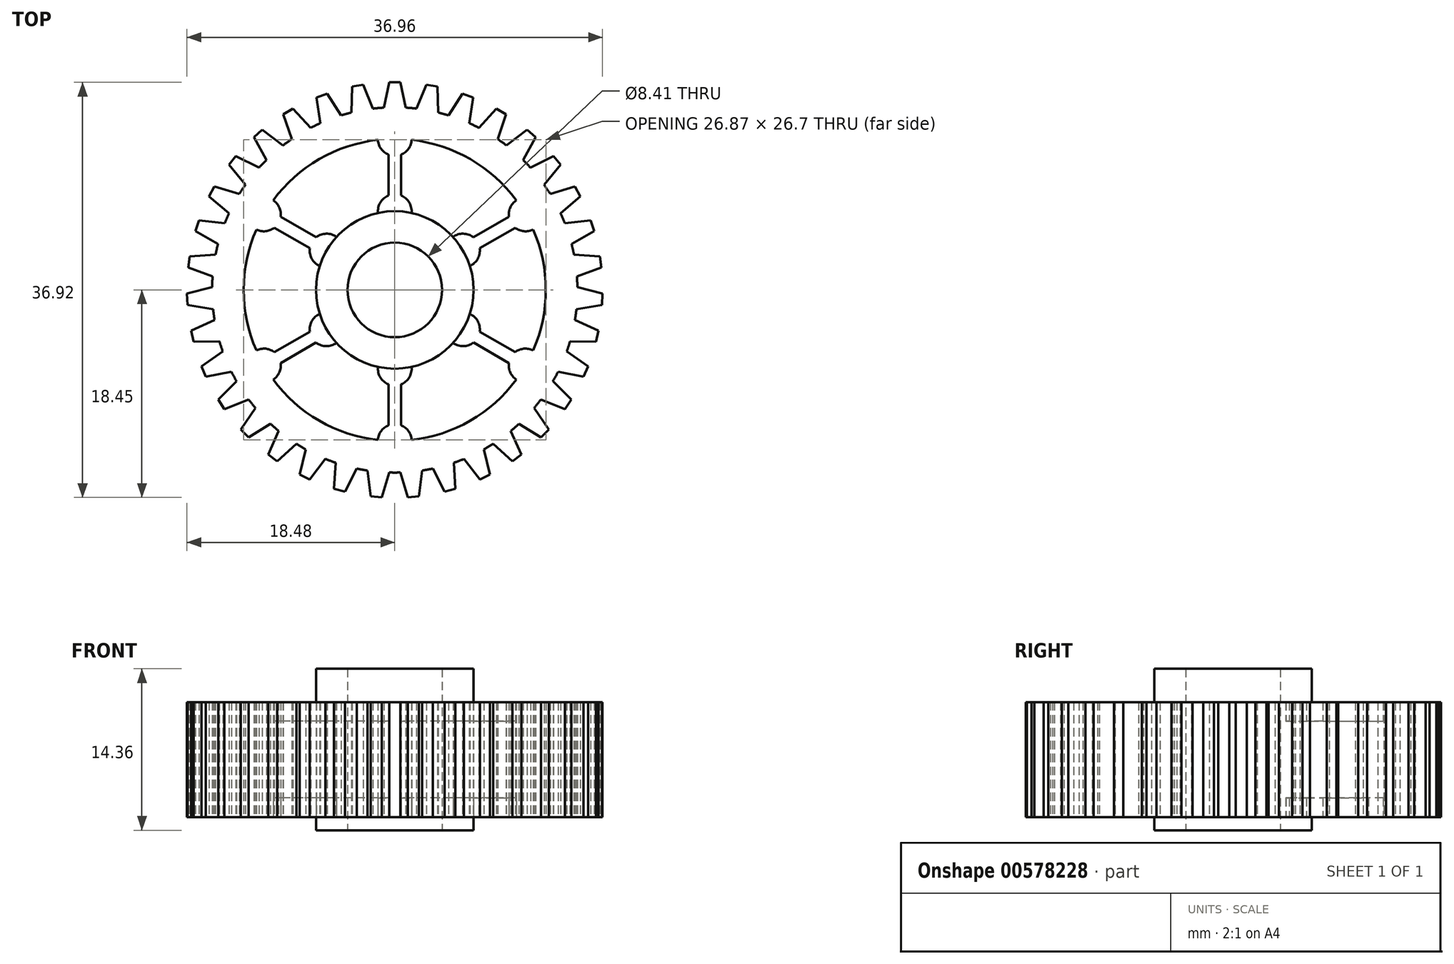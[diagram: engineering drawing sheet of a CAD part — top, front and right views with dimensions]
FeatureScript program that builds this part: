
annotation { "Feature Type Name" : "Feature", "Feature Type Description" : "" }
export const myFeature = defineFeature(function(context is Context, id is Id, definition is map)
    precondition{}
    {
        {
            var Q0;
            Q0=qCreatedBy(makeId("Top.planeOp"),FACE);
            var sketch = newSketch(context, id + "F0", { "sketchPlane" : qUnion([Q0])});
            skCircle(sketch, "E0", {"center": v(0, 0) * mm, "radius": 4.2 * mm});
            skCircle(sketch, "E1.0", {"center": v(0, 0) * mm, "radius": 7 * mm});
            skCircle(sketch, "E2.0", {"center": v(0, 0) * mm, "radius": 16.24 * mm});
            skCircle(sketch, "E3.0", {"center": v(0, 0) * mm, "radius": 13.43 * mm});
            skLineSegment(sketch, "E4", {"start": v(0, 0) * mm, "end": v(0, 25.5) * mm, "construction": true});
            skLineSegment(sketch, "E5", {"start": v(0, 13.43) * mm, "end": v(0, 18.47) * mm});
            skLineSegment(sketch, "E6", {"start": v(0, 18.47) * mm, "end": v(-0.5, 18.47) * mm});
            skLineSegment(sketch, "E7", {"start": v(-0.5, 18.47) * mm, "end": v(-0.98, 16.22) * mm});
            skLineSegment(sketch, "E8", {"start": v(0, 18.47) * mm, "end": v(0.5, 18.47) * mm});
            skLineSegment(sketch, "E9", {"start": v(0.5, 18.47) * mm, "end": v(0.97, 16.22) * mm});
            skLineSegment(sketch, "E10.1.0", {"start": v(-2.8, 18.27) * mm, "end": v(-1.94, 16.13) * mm});
            skLineSegment(sketch, "E10.1.1", {"start": v(-3.3, 18.18) * mm, "end": v(-2.8, 18.27) * mm});
            skLineSegment(sketch, "E10.1.2", {"start": v(-3.3, 18.18) * mm, "end": v(-3.8, 18.09) * mm});
            skLineSegment(sketch, "E10.1.3", {"start": v(-3.8, 18.09) * mm, "end": v(-3.85, 15.78) * mm});
            skLineSegment(sketch, "E10.2.0", {"start": v(-6.02, 17.47) * mm, "end": v(-4.78, 15.52) * mm});
            skLineSegment(sketch, "E10.2.1", {"start": v(-6.5, 17.3) * mm, "end": v(-6.02, 17.47) * mm});
            skLineSegment(sketch, "E10.2.2", {"start": v(-6.5, 17.3) * mm, "end": v(-6.96, 17.12) * mm});
            skLineSegment(sketch, "E10.2.3", {"start": v(-6.96, 17.12) * mm, "end": v(-6.61, 14.84) * mm});
            skLineSegment(sketch, "E10.3.0", {"start": v(-9.05, 16.12) * mm, "end": v(-7.48, 14.42) * mm});
            skLineSegment(sketch, "E10.3.1", {"start": v(-9.48, 15.86) * mm, "end": v(-9.05, 16.12) * mm});
            skLineSegment(sketch, "E10.3.2", {"start": v(-9.48, 15.86) * mm, "end": v(-9.9, 15.6) * mm});
            skLineSegment(sketch, "E10.3.3", {"start": v(-9.9, 15.6) * mm, "end": v(-9.15, 13.42) * mm});
            skLineSegment(sketch, "E10.4.0", {"start": v(-11.78, 14.24) * mm, "end": v(-9.93, 12.85) * mm});
            skLineSegment(sketch, "E10.4.1", {"start": v(-12.16, 13.91) * mm, "end": v(-11.78, 14.24) * mm});
            skLineSegment(sketch, "E10.4.2", {"start": v(-12.16, 13.91) * mm, "end": v(-12.53, 13.58) * mm});
            skLineSegment(sketch, "E10.4.3", {"start": v(-12.53, 13.58) * mm, "end": v(-11.4, 11.57) * mm});
            skLineSegment(sketch, "E10.5.0", {"start": v(-14.13, 11.9) * mm, "end": v(-12.07, 10.87) * mm});
            skLineSegment(sketch, "E10.5.1", {"start": v(-14.44, 11.52) * mm, "end": v(-14.13, 11.9) * mm});
            skLineSegment(sketch, "E10.5.2", {"start": v(-14.44, 11.52) * mm, "end": v(-14.76, 11.13) * mm});
            skLineSegment(sketch, "E10.5.3", {"start": v(-14.76, 11.13) * mm, "end": v(-13.29, 9.35) * mm});
            skLineSegment(sketch, "E10.6.0", {"start": v(-16.03, 9.2) * mm, "end": v(-13.82, 8.54) * mm});
            skLineSegment(sketch, "E10.6.1", {"start": v(-16.27, 8.75) * mm, "end": v(-16.03, 9.2) * mm});
            skLineSegment(sketch, "E10.6.2", {"start": v(-16.27, 8.75) * mm, "end": v(-16.5, 8.31) * mm});
            skLineSegment(sketch, "E10.6.3", {"start": v(-16.5, 8.31) * mm, "end": v(-14.74, 6.83) * mm});
            skLineSegment(sketch, "E10.7.0", {"start": v(-17.42, 6.18) * mm, "end": v(-15.12, 5.94) * mm});
            skLineSegment(sketch, "E10.7.1", {"start": v(-17.57, 5.7) * mm, "end": v(-17.42, 6.18) * mm});
            skLineSegment(sketch, "E10.7.2", {"start": v(-17.57, 5.7) * mm, "end": v(-17.73, 5.23) * mm});
            skLineSegment(sketch, "E10.7.3", {"start": v(-17.73, 5.23) * mm, "end": v(-15.72, 4.08) * mm});
            skLineSegment(sketch, "E10.8.0", {"start": v(-18.24, 2.98) * mm, "end": v(-15.94, 3.14) * mm});
            skLineSegment(sketch, "E10.8.1", {"start": v(-18.3, 2.48) * mm, "end": v(-18.24, 2.98) * mm});
            skLineSegment(sketch, "E10.8.2", {"start": v(-18.3, 2.48) * mm, "end": v(-18.37, 1.98) * mm});
            skLineSegment(sketch, "E10.8.3", {"start": v(-18.37, 1.98) * mm, "end": v(-16.2, 1.21) * mm});
            skLineSegment(sketch, "E10.9.0", {"start": v(-18.48, -0.33) * mm, "end": v(-16.24, 0.25) * mm});
            skLineSegment(sketch, "E10.9.1", {"start": v(-18.46, -0.83) * mm, "end": v(-18.48, -0.33) * mm});
            skLineSegment(sketch, "E10.9.2", {"start": v(-18.46, -0.83) * mm, "end": v(-18.43, -1.33) * mm});
            skLineSegment(sketch, "E10.9.3", {"start": v(-18.43, -1.33) * mm, "end": v(-16.16, -1.7) * mm});
            skLineSegment(sketch, "E10.10.0", {"start": v(-18.12, -3.62) * mm, "end": v(-16.03, -2.66) * mm});
            skLineSegment(sketch, "E10.10.1", {"start": v(-18.01, -4.11) * mm, "end": v(-18.12, -3.62) * mm});
            skLineSegment(sketch, "E10.10.2", {"start": v(-18.01, -4.11) * mm, "end": v(-17.9, -4.6) * mm});
            skLineSegment(sketch, "E10.10.3", {"start": v(-17.9, -4.6) * mm, "end": v(-15.6, -4.56) * mm});
            skLineSegment(sketch, "E10.11.0", {"start": v(-17.18, -6.8) * mm, "end": v(-15.3, -5.48) * mm});
            skLineSegment(sketch, "E10.11.1", {"start": v(-16.99, -7.26) * mm, "end": v(-17.18, -6.8) * mm});
            skLineSegment(sketch, "E10.11.2", {"start": v(-16.99, -7.26) * mm, "end": v(-16.8, -7.72) * mm});
            skLineSegment(sketch, "E10.11.3", {"start": v(-16.8, -7.72) * mm, "end": v(-14.53, -7.27) * mm});
            skLineSegment(sketch, "E10.12.0", {"start": v(-15.7, -9.76) * mm, "end": v(-14.07, -8.12) * mm});
            skLineSegment(sketch, "E10.12.1", {"start": v(-15.42, -10.18) * mm, "end": v(-15.7, -9.76) * mm});
            skLineSegment(sketch, "E10.12.2", {"start": v(-15.42, -10.18) * mm, "end": v(-15.14, -10.6) * mm});
            skLineSegment(sketch, "E10.12.3", {"start": v(-15.14, -10.6) * mm, "end": v(-13, -9.75) * mm});
            skLineSegment(sketch, "E10.13.0", {"start": v(-13.7, -12.4) * mm, "end": v(-12.4, -10.5) * mm});
            skLineSegment(sketch, "E10.13.1", {"start": v(-13.35, -12.77) * mm, "end": v(-13.7, -12.4) * mm});
            skLineSegment(sketch, "E10.13.2", {"start": v(-13.35, -12.77) * mm, "end": v(-13, -13.13) * mm});
            skLineSegment(sketch, "E10.13.3", {"start": v(-13, -13.13) * mm, "end": v(-11.05, -11.91) * mm});
            skLineSegment(sketch, "E10.14.0", {"start": v(-11.26, -14.65) * mm, "end": v(-10.32, -12.55) * mm});
            skLineSegment(sketch, "E10.14.1", {"start": v(-10.86, -14.95) * mm, "end": v(-11.26, -14.65) * mm});
            skLineSegment(sketch, "E10.14.2", {"start": v(-10.86, -14.95) * mm, "end": v(-10.45, -15.24) * mm});
            skLineSegment(sketch, "E10.14.3", {"start": v(-10.45, -15.24) * mm, "end": v(-8.74, -13.7) * mm});
            skLineSegment(sketch, "E10.15.0", {"start": v(-8.47, -16.43) * mm, "end": v(-7.91, -14.19) * mm});
            skLineSegment(sketch, "E10.15.1", {"start": v(-8.02, -16.65) * mm, "end": v(-8.47, -16.43) * mm});
            skLineSegment(sketch, "E10.15.2", {"start": v(-8.02, -16.65) * mm, "end": v(-7.57, -16.86) * mm});
            skLineSegment(sketch, "E10.15.3", {"start": v(-7.57, -16.86) * mm, "end": v(-6.16, -15.03) * mm});
            skLineSegment(sketch, "E10.16.0", {"start": v(-5.4, -17.68) * mm, "end": v(-5.25, -15.37) * mm});
            skLineSegment(sketch, "E10.16.1", {"start": v(-4.92, -17.8) * mm, "end": v(-5.4, -17.68) * mm});
            skLineSegment(sketch, "E10.16.2", {"start": v(-4.92, -17.8) * mm, "end": v(-4.43, -17.94) * mm});
            skLineSegment(sketch, "E10.16.3", {"start": v(-4.43, -17.94) * mm, "end": v(-3.37, -15.9) * mm});
            skLineSegment(sketch, "E10.17.0", {"start": v(-2.15, -18.36) * mm, "end": v(-2.42, -16.06) * mm});
            skLineSegment(sketch, "E10.17.1", {"start": v(-1.66, -18.4) * mm, "end": v(-2.15, -18.36) * mm});
            skLineSegment(sketch, "E10.17.2", {"start": v(-1.66, -18.4) * mm, "end": v(-1.16, -18.45) * mm});
            skLineSegment(sketch, "E10.17.3", {"start": v(-1.16, -18.45) * mm, "end": v(-0.48, -16.24) * mm});
            skLineSegment(sketch, "E10.18.0", {"start": v(1.16, -18.45) * mm, "end": v(0.48, -16.24) * mm});
            skLineSegment(sketch, "E10.18.1", {"start": v(1.66, -18.4) * mm, "end": v(1.16, -18.45) * mm});
            skLineSegment(sketch, "E10.18.2", {"start": v(1.66, -18.4) * mm, "end": v(2.15, -18.36) * mm});
            skLineSegment(sketch, "E10.18.3", {"start": v(2.15, -18.36) * mm, "end": v(2.42, -16.06) * mm});
            skLineSegment(sketch, "E10.19.0", {"start": v(4.43, -17.94) * mm, "end": v(3.37, -15.9) * mm});
            skLineSegment(sketch, "E10.19.1", {"start": v(4.92, -17.8) * mm, "end": v(4.43, -17.94) * mm});
            skLineSegment(sketch, "E10.19.2", {"start": v(4.92, -17.8) * mm, "end": v(5.4, -17.68) * mm});
            skLineSegment(sketch, "E10.19.3", {"start": v(5.4, -17.68) * mm, "end": v(5.25, -15.37) * mm});
            skLineSegment(sketch, "E10.20.0", {"start": v(7.57, -16.86) * mm, "end": v(6.16, -15.03) * mm});
            skLineSegment(sketch, "E10.20.1", {"start": v(8.02, -16.65) * mm, "end": v(7.57, -16.86) * mm});
            skLineSegment(sketch, "E10.20.2", {"start": v(8.02, -16.65) * mm, "end": v(8.47, -16.43) * mm});
            skLineSegment(sketch, "E10.20.3", {"start": v(8.47, -16.43) * mm, "end": v(7.91, -14.19) * mm});
            skLineSegment(sketch, "E10.21.0", {"start": v(10.45, -15.24) * mm, "end": v(8.74, -13.7) * mm});
            skLineSegment(sketch, "E10.21.1", {"start": v(10.86, -14.95) * mm, "end": v(10.45, -15.24) * mm});
            skLineSegment(sketch, "E10.21.2", {"start": v(10.86, -14.95) * mm, "end": v(11.26, -14.65) * mm});
            skLineSegment(sketch, "E10.21.3", {"start": v(11.26, -14.65) * mm, "end": v(10.32, -12.55) * mm});
            skLineSegment(sketch, "E10.22.0", {"start": v(13, -13.13) * mm, "end": v(11.05, -11.91) * mm});
            skLineSegment(sketch, "E10.22.1", {"start": v(13.35, -12.77) * mm, "end": v(13, -13.13) * mm});
            skLineSegment(sketch, "E10.22.2", {"start": v(13.35, -12.77) * mm, "end": v(13.7, -12.4) * mm});
            skLineSegment(sketch, "E10.22.3", {"start": v(13.7, -12.4) * mm, "end": v(12.4, -10.5) * mm});
            skLineSegment(sketch, "E10.23.0", {"start": v(15.14, -10.6) * mm, "end": v(13, -9.75) * mm});
            skLineSegment(sketch, "E10.23.1", {"start": v(15.42, -10.18) * mm, "end": v(15.14, -10.6) * mm});
            skLineSegment(sketch, "E10.23.2", {"start": v(15.42, -10.18) * mm, "end": v(15.7, -9.76) * mm});
            skLineSegment(sketch, "E10.23.3", {"start": v(15.7, -9.76) * mm, "end": v(14.07, -8.12) * mm});
            skLineSegment(sketch, "E10.24.0", {"start": v(16.8, -7.72) * mm, "end": v(14.53, -7.27) * mm});
            skLineSegment(sketch, "E10.24.1", {"start": v(16.99, -7.26) * mm, "end": v(16.8, -7.72) * mm});
            skLineSegment(sketch, "E10.24.2", {"start": v(16.99, -7.26) * mm, "end": v(17.18, -6.8) * mm});
            skLineSegment(sketch, "E10.24.3", {"start": v(17.18, -6.8) * mm, "end": v(15.3, -5.48) * mm});
            skLineSegment(sketch, "E10.25.0", {"start": v(17.9, -4.6) * mm, "end": v(15.6, -4.56) * mm});
            skLineSegment(sketch, "E10.25.1", {"start": v(18.01, -4.11) * mm, "end": v(17.9, -4.6) * mm});
            skLineSegment(sketch, "E10.25.2", {"start": v(18.01, -4.11) * mm, "end": v(18.12, -3.62) * mm});
            skLineSegment(sketch, "E10.25.3", {"start": v(18.12, -3.62) * mm, "end": v(16.03, -2.66) * mm});
            skLineSegment(sketch, "E10.26.0", {"start": v(18.43, -1.33) * mm, "end": v(16.16, -1.7) * mm});
            skLineSegment(sketch, "E10.26.1", {"start": v(18.46, -0.83) * mm, "end": v(18.43, -1.33) * mm});
            skLineSegment(sketch, "E10.26.2", {"start": v(18.46, -0.83) * mm, "end": v(18.48, -0.33) * mm});
            skLineSegment(sketch, "E10.26.3", {"start": v(18.48, -0.33) * mm, "end": v(16.24, 0.25) * mm});
            skLineSegment(sketch, "E10.27.0", {"start": v(18.37, 1.98) * mm, "end": v(16.2, 1.21) * mm});
            skLineSegment(sketch, "E10.27.1", {"start": v(18.3, 2.48) * mm, "end": v(18.37, 1.98) * mm});
            skLineSegment(sketch, "E10.27.2", {"start": v(18.3, 2.48) * mm, "end": v(18.24, 2.98) * mm});
            skLineSegment(sketch, "E10.27.3", {"start": v(18.24, 2.98) * mm, "end": v(15.94, 3.14) * mm});
            skLineSegment(sketch, "E10.28.0", {"start": v(17.73, 5.23) * mm, "end": v(15.72, 4.08) * mm});
            skLineSegment(sketch, "E10.28.1", {"start": v(17.57, 5.7) * mm, "end": v(17.73, 5.23) * mm});
            skLineSegment(sketch, "E10.28.2", {"start": v(17.57, 5.7) * mm, "end": v(17.42, 6.18) * mm});
            skLineSegment(sketch, "E10.28.3", {"start": v(17.42, 6.18) * mm, "end": v(15.12, 5.94) * mm});
            skLineSegment(sketch, "E10.29.0", {"start": v(16.5, 8.31) * mm, "end": v(14.74, 6.83) * mm});
            skLineSegment(sketch, "E10.29.1", {"start": v(16.27, 8.75) * mm, "end": v(16.5, 8.31) * mm});
            skLineSegment(sketch, "E10.29.2", {"start": v(16.27, 8.75) * mm, "end": v(16.03, 9.2) * mm});
            skLineSegment(sketch, "E10.29.3", {"start": v(16.03, 9.2) * mm, "end": v(13.82, 8.54) * mm});
            skLineSegment(sketch, "E10.30.0", {"start": v(14.76, 11.13) * mm, "end": v(13.29, 9.35) * mm});
            skLineSegment(sketch, "E10.30.1", {"start": v(14.44, 11.52) * mm, "end": v(14.76, 11.13) * mm});
            skLineSegment(sketch, "E10.30.2", {"start": v(14.44, 11.52) * mm, "end": v(14.13, 11.9) * mm});
            skLineSegment(sketch, "E10.30.3", {"start": v(14.13, 11.9) * mm, "end": v(12.07, 10.87) * mm});
            skLineSegment(sketch, "E10.31.0", {"start": v(12.53, 13.58) * mm, "end": v(11.4, 11.57) * mm});
            skLineSegment(sketch, "E10.31.1", {"start": v(12.16, 13.91) * mm, "end": v(12.53, 13.58) * mm});
            skLineSegment(sketch, "E10.31.2", {"start": v(12.16, 13.91) * mm, "end": v(11.78, 14.24) * mm});
            skLineSegment(sketch, "E10.31.3", {"start": v(11.78, 14.24) * mm, "end": v(9.93, 12.85) * mm});
            skLineSegment(sketch, "E10.32.0", {"start": v(9.9, 15.6) * mm, "end": v(9.15, 13.42) * mm});
            skLineSegment(sketch, "E10.32.1", {"start": v(9.48, 15.86) * mm, "end": v(9.9, 15.6) * mm});
            skLineSegment(sketch, "E10.32.2", {"start": v(9.48, 15.86) * mm, "end": v(9.05, 16.12) * mm});
            skLineSegment(sketch, "E10.32.3", {"start": v(9.05, 16.12) * mm, "end": v(7.48, 14.42) * mm});
            skLineSegment(sketch, "E10.33.0", {"start": v(6.96, 17.12) * mm, "end": v(6.61, 14.84) * mm});
            skLineSegment(sketch, "E10.33.1", {"start": v(6.5, 17.3) * mm, "end": v(6.96, 17.12) * mm});
            skLineSegment(sketch, "E10.33.2", {"start": v(6.5, 17.3) * mm, "end": v(6.02, 17.47) * mm});
            skLineSegment(sketch, "E10.33.3", {"start": v(6.02, 17.47) * mm, "end": v(4.78, 15.52) * mm});
            skLineSegment(sketch, "E10.34.0", {"start": v(3.8, 18.09) * mm, "end": v(3.85, 15.78) * mm});
            skLineSegment(sketch, "E10.34.1", {"start": v(3.3, 18.18) * mm, "end": v(3.8, 18.09) * mm});
            skLineSegment(sketch, "E10.34.2", {"start": v(3.3, 18.18) * mm, "end": v(2.8, 18.27) * mm});
            skLineSegment(sketch, "E10.34.3", {"start": v(2.8, 18.27) * mm, "end": v(1.94, 16.13) * mm});
            skLineSegment(sketch, "E11.left", {"start": v(-0.56, 8.4) * mm, "end": v(-0.56, 12.04) * mm});
            skLineSegment(sketch, "E11.right", {"start": v(0.56, 8.4) * mm, "end": v(0.56, 12.04) * mm});
            skPoint(sketch, "E11.middle", {"position": v(0, 10.27) * mm});
            skArc(sketch, "E12", {"start": v(-1.5, 13.35) * mm, "mid": v(-1.22, 12.56) * mm, "end": v(-0.56, 12.04) * mm});
            skArc(sketch, "E13.trimOffspring", {"start": v(0.56, 12.04) * mm, "mid": v(1.22, 12.56) * mm, "end": v(1.5, 13.35) * mm});
            skArc(sketch, "E14", {"start": v(-1.5, 6.84) * mm, "mid": v(-1.29, 7.78) * mm, "end": v(-0.56, 8.4) * mm});
            skArc(sketch, "E15.trimOffspring", {"start": v(0.56, 8.4) * mm, "mid": v(1.29, 7.78) * mm, "end": v(1.5, 6.84) * mm});
            skArc(sketch, "E16.1.0", {"start": v(-10.15, 6.5) * mm, "mid": v(-10.27, 7.34) * mm, "end": v(-10.81, 7.97) * mm});
            skLineSegment(sketch, "E16.1.1", {"start": v(-7, 4.68) * mm, "end": v(-10.15, 6.5) * mm});
            skArc(sketch, "E16.1.2", {"start": v(-7, 4.68) * mm, "mid": v(-6.1, 5) * mm, "end": v(-5.18, 4.71) * mm});
            skArc(sketch, "E16.1.3", {"start": v(-6.67, 2.13) * mm, "mid": v(-7.38, 2.77) * mm, "end": v(-7.55, 3.71) * mm});
            skLineSegment(sketch, "E16.1.4", {"start": v(-7.55, 3.71) * mm, "end": v(-10.7, 5.54) * mm});
            skArc(sketch, "E16.1.5", {"start": v(-12.31, 5.38) * mm, "mid": v(-11.49, 5.22) * mm, "end": v(-10.7, 5.54) * mm});
            skArc(sketch, "E16.2.0", {"start": v(-10.7, -5.54) * mm, "mid": v(-11.49, -5.22) * mm, "end": v(-12.31, -5.38) * mm});
            skLineSegment(sketch, "E16.2.1", {"start": v(-7.55, -3.71) * mm, "end": v(-10.7, -5.54) * mm});
            skArc(sketch, "E16.2.2", {"start": v(-7.55, -3.71) * mm, "mid": v(-7.38, -2.77) * mm, "end": v(-6.67, -2.13) * mm});
            skArc(sketch, "E16.2.3", {"start": v(-5.18, -4.71) * mm, "mid": v(-6.1, -5) * mm, "end": v(-7, -4.68) * mm});
            skLineSegment(sketch, "E16.2.4", {"start": v(-7, -4.68) * mm, "end": v(-10.15, -6.5) * mm});
            skArc(sketch, "E16.2.5", {"start": v(-10.81, -7.97) * mm, "mid": v(-10.27, -7.34) * mm, "end": v(-10.15, -6.5) * mm});
            skArc(sketch, "E16.3.0", {"start": v(-0.56, -12.04) * mm, "mid": v(-1.22, -12.56) * mm, "end": v(-1.5, -13.35) * mm});
            skLineSegment(sketch, "E16.3.1", {"start": v(-0.56, -8.4) * mm, "end": v(-0.56, -12.04) * mm});
            skArc(sketch, "E16.3.2", {"start": v(-0.56, -8.4) * mm, "mid": v(-1.29, -7.78) * mm, "end": v(-1.5, -6.84) * mm});
            skArc(sketch, "E16.3.3", {"start": v(1.5, -6.84) * mm, "mid": v(1.29, -7.78) * mm, "end": v(0.56, -8.4) * mm});
            skLineSegment(sketch, "E16.3.4", {"start": v(0.56, -8.4) * mm, "end": v(0.56, -12.04) * mm});
            skArc(sketch, "E16.3.5", {"start": v(1.5, -13.35) * mm, "mid": v(1.22, -12.56) * mm, "end": v(0.56, -12.04) * mm});
            skArc(sketch, "E16.4.0", {"start": v(10.15, -6.5) * mm, "mid": v(10.27, -7.34) * mm, "end": v(10.81, -7.97) * mm});
            skLineSegment(sketch, "E16.4.1", {"start": v(7, -4.68) * mm, "end": v(10.15, -6.5) * mm});
            skArc(sketch, "E16.4.2", {"start": v(7, -4.68) * mm, "mid": v(6.1, -5) * mm, "end": v(5.18, -4.71) * mm});
            skArc(sketch, "E16.4.3", {"start": v(6.67, -2.13) * mm, "mid": v(7.38, -2.77) * mm, "end": v(7.55, -3.71) * mm});
            skLineSegment(sketch, "E16.4.4", {"start": v(7.55, -3.71) * mm, "end": v(10.7, -5.54) * mm});
            skArc(sketch, "E16.4.5", {"start": v(12.31, -5.38) * mm, "mid": v(11.49, -5.22) * mm, "end": v(10.7, -5.54) * mm});
            skArc(sketch, "E16.5.0", {"start": v(10.7, 5.54) * mm, "mid": v(11.49, 5.22) * mm, "end": v(12.31, 5.38) * mm});
            skLineSegment(sketch, "E16.5.1", {"start": v(7.55, 3.71) * mm, "end": v(10.7, 5.54) * mm});
            skArc(sketch, "E16.5.2", {"start": v(7.55, 3.71) * mm, "mid": v(7.38, 2.77) * mm, "end": v(6.67, 2.13) * mm});
            skArc(sketch, "E16.5.3", {"start": v(5.18, 4.71) * mm, "mid": v(6.1, 5) * mm, "end": v(7, 4.68) * mm});
            skLineSegment(sketch, "E16.5.4", {"start": v(7, 4.68) * mm, "end": v(10.15, 6.5) * mm});
            skArc(sketch, "E16.5.5", {"start": v(10.81, 7.97) * mm, "mid": v(10.27, 7.34) * mm, "end": v(10.15, 6.5) * mm});
            skSolve(sketch);
        }
        {
            var Q0;
            {var subQ72=sQuery(id+"F0.wireOp",EDGE,"E3.0");var subQ76=makeQuery(id+"F0.imprint","IMPRINT",VERTEX,{"derivedFrom":subQ72});Q0=makeQuery(id+"F0.imprint","IMPRINT",FACE,{"disambiguationData":[TD([[makeQuery(id+"F0.imprint","IMPRINT",EDGE,{"disambiguationData":[TD([[subQ76,1.0]])],"derivedFrom":subQ72}),-1.0]])]});}
            var Q1;
            {var subQ0=sQuery(id+"F0.wireOp",EDGE,"E16.1.0");Q1=makeQuery(id+"F0.imprint","IMPRINT",FACE,{"disambiguationData":[TD([[makeQuery(id+"F0.imprint","IMPRINT",EDGE,{"derivedFrom":subQ0}),1.0]])]});}
            var Q2;
            Q2=makeQuery(id+"F0.imprint","IMPRINT",FACE,{"disambiguationData":[TD([[makeQuery(id+"F0.imprint","IMPRINT",EDGE,{"derivedFrom":sQuery(id+"F0.wireOp",EDGE,"E11.left")}),-1.0]])]});
            var Q3;
            {var subQ0=sQuery(id+"F0.wireOp",EDGE,"E16.5.0");Q3=makeQuery(id+"F0.imprint","IMPRINT",FACE,{"disambiguationData":[TD([[makeQuery(id+"F0.imprint","IMPRINT",EDGE,{"derivedFrom":subQ0}),1.0]])]});}
            var Q4;
            {var subQ0=sQuery(id+"F0.wireOp",EDGE,"E16.4.0");Q4=makeQuery(id+"F0.imprint","IMPRINT",FACE,{"disambiguationData":[TD([[makeQuery(id+"F0.imprint","IMPRINT",EDGE,{"derivedFrom":subQ0}),1.0]])]});}
            var Q5;
            {var subQ0=sQuery(id+"F0.wireOp",EDGE,"E16.3.0");Q5=makeQuery(id+"F0.imprint","IMPRINT",FACE,{"disambiguationData":[TD([[makeQuery(id+"F0.imprint","IMPRINT",EDGE,{"derivedFrom":subQ0}),1.0]])]});}
            var Q6;
            {var subQ0=sQuery(id+"F0.wireOp",EDGE,"E16.2.0");Q6=makeQuery(id+"F0.imprint","IMPRINT",FACE,{"disambiguationData":[TD([[makeQuery(id+"F0.imprint","IMPRINT",EDGE,{"derivedFrom":subQ0}),1.0]])]});}
            var Q7;
            Q7=makeQuery(id+"F0.imprint","IMPRINT",FACE,{"disambiguationData":[TD([[makeQuery(id+"F0.imprint","IMPRINT",EDGE,{"derivedFrom":sQuery(id+"F0.wireOp",EDGE,"E0")}),-1.0]])]});
            var Q8;
            {var subQ0=sQuery(id+"F0.wireOp",EDGE,"E10.5.0");Q8=makeQuery(id+"F0.imprint","IMPRINT",FACE,{"disambiguationData":[TD([[makeQuery(id+"F0.imprint","IMPRINT",EDGE,{"derivedFrom":subQ0}),-1.0]])]});}
            var Q9;
            {var subQ0=sQuery(id+"F0.wireOp",EDGE,"E10.4.0");Q9=makeQuery(id+"F0.imprint","IMPRINT",FACE,{"disambiguationData":[TD([[makeQuery(id+"F0.imprint","IMPRINT",EDGE,{"derivedFrom":subQ0}),-1.0]])]});}
            var Q10;
            {var subQ0=sQuery(id+"F0.wireOp",EDGE,"E10.3.0");Q10=makeQuery(id+"F0.imprint","IMPRINT",FACE,{"disambiguationData":[TD([[makeQuery(id+"F0.imprint","IMPRINT",EDGE,{"derivedFrom":subQ0}),-1.0]])]});}
            var Q11;
            {var subQ0=sQuery(id+"F0.wireOp",EDGE,"E10.2.0");Q11=makeQuery(id+"F0.imprint","IMPRINT",FACE,{"disambiguationData":[TD([[makeQuery(id+"F0.imprint","IMPRINT",EDGE,{"derivedFrom":subQ0}),-1.0]])]});}
            var Q12;
            {var subQ0=sQuery(id+"F0.wireOp",EDGE,"E10.1.0");Q12=makeQuery(id+"F0.imprint","IMPRINT",FACE,{"disambiguationData":[TD([[makeQuery(id+"F0.imprint","IMPRINT",EDGE,{"derivedFrom":subQ0}),-1.0]])]});}
            var Q13;
            {var subQ0=sQuery(id+"F0.wireOp",EDGE,"E10.9.0");Q13=makeQuery(id+"F0.imprint","IMPRINT",FACE,{"disambiguationData":[TD([[makeQuery(id+"F0.imprint","IMPRINT",EDGE,{"derivedFrom":subQ0}),-1.0]])]});}
            var Q14;
            {var subQ0=sQuery(id+"F0.wireOp",EDGE,"E10.10.0");Q14=makeQuery(id+"F0.imprint","IMPRINT",FACE,{"disambiguationData":[TD([[makeQuery(id+"F0.imprint","IMPRINT",EDGE,{"derivedFrom":subQ0}),-1.0]])]});}
            var Q15;
            {var subQ0=sQuery(id+"F0.wireOp",EDGE,"E10.16.0");Q15=makeQuery(id+"F0.imprint","IMPRINT",FACE,{"disambiguationData":[TD([[makeQuery(id+"F0.imprint","IMPRINT",EDGE,{"derivedFrom":subQ0}),-1.0]])]});}
            var Q16;
            {var subQ0=sQuery(id+"F0.wireOp",EDGE,"E10.11.0");Q16=makeQuery(id+"F0.imprint","IMPRINT",FACE,{"disambiguationData":[TD([[makeQuery(id+"F0.imprint","IMPRINT",EDGE,{"derivedFrom":subQ0}),-1.0]])]});}
            var Q17;
            {var subQ0=sQuery(id+"F0.wireOp",EDGE,"E10.26.0");Q17=makeQuery(id+"F0.imprint","IMPRINT",FACE,{"disambiguationData":[TD([[makeQuery(id+"F0.imprint","IMPRINT",EDGE,{"derivedFrom":subQ0}),-1.0]])]});}
            var Q18;
            {var subQ4=sQuery(id+"F0.wireOp",EDGE,"E8");Q18=makeQuery(id+"F0.imprint","IMPRINT",FACE,{"disambiguationData":[TD([[makeQuery(id+"F0.imprint","IMPRINT",EDGE,{"derivedFrom":subQ4}),-1.0]])]});}
            var Q19;
            {var subQ0=sQuery(id+"F0.wireOp",EDGE,"E10.25.0");Q19=makeQuery(id+"F0.imprint","IMPRINT",FACE,{"disambiguationData":[TD([[makeQuery(id+"F0.imprint","IMPRINT",EDGE,{"derivedFrom":subQ0}),-1.0]])]});}
            var Q20;
            {var subQ0=sQuery(id+"F0.wireOp",EDGE,"E10.12.0");Q20=makeQuery(id+"F0.imprint","IMPRINT",FACE,{"disambiguationData":[TD([[makeQuery(id+"F0.imprint","IMPRINT",EDGE,{"derivedFrom":subQ0}),-1.0]])]});}
            var Q21;
            {var subQ4=sQuery(id+"F0.wireOp",EDGE,"E6");Q21=makeQuery(id+"F0.imprint","IMPRINT",FACE,{"disambiguationData":[TD([[makeQuery(id+"F0.imprint","IMPRINT",EDGE,{"derivedFrom":subQ4}),1.0]])]});}
            var Q22;
            {var subQ0=sQuery(id+"F0.wireOp",EDGE,"E10.20.0");Q22=makeQuery(id+"F0.imprint","IMPRINT",FACE,{"disambiguationData":[TD([[makeQuery(id+"F0.imprint","IMPRINT",EDGE,{"derivedFrom":subQ0}),-1.0]])]});}
            var Q23;
            {var subQ0=sQuery(id+"F0.wireOp",EDGE,"E10.13.0");Q23=makeQuery(id+"F0.imprint","IMPRINT",FACE,{"disambiguationData":[TD([[makeQuery(id+"F0.imprint","IMPRINT",EDGE,{"derivedFrom":subQ0}),-1.0]])]});}
            var Q24;
            {var subQ0=sQuery(id+"F0.wireOp",EDGE,"E10.7.0");Q24=makeQuery(id+"F0.imprint","IMPRINT",FACE,{"disambiguationData":[TD([[makeQuery(id+"F0.imprint","IMPRINT",EDGE,{"derivedFrom":subQ0}),-1.0]])]});}
            var Q25;
            {var subQ0=sQuery(id+"F0.wireOp",EDGE,"E10.14.0");Q25=makeQuery(id+"F0.imprint","IMPRINT",FACE,{"disambiguationData":[TD([[makeQuery(id+"F0.imprint","IMPRINT",EDGE,{"derivedFrom":subQ0}),-1.0]])]});}
            var Q26;
            {var subQ0=sQuery(id+"F0.wireOp",EDGE,"E10.30.0");Q26=makeQuery(id+"F0.imprint","IMPRINT",FACE,{"disambiguationData":[TD([[makeQuery(id+"F0.imprint","IMPRINT",EDGE,{"derivedFrom":subQ0}),-1.0]])]});}
            var Q27;
            {var subQ0=sQuery(id+"F0.wireOp",EDGE,"E10.28.0");Q27=makeQuery(id+"F0.imprint","IMPRINT",FACE,{"disambiguationData":[TD([[makeQuery(id+"F0.imprint","IMPRINT",EDGE,{"derivedFrom":subQ0}),-1.0]])]});}
            var Q28;
            {var subQ0=sQuery(id+"F0.wireOp",EDGE,"E10.24.0");Q28=makeQuery(id+"F0.imprint","IMPRINT",FACE,{"disambiguationData":[TD([[makeQuery(id+"F0.imprint","IMPRINT",EDGE,{"derivedFrom":subQ0}),-1.0]])]});}
            var Q29;
            {var subQ0=sQuery(id+"F0.wireOp",EDGE,"E10.8.0");Q29=makeQuery(id+"F0.imprint","IMPRINT",FACE,{"disambiguationData":[TD([[makeQuery(id+"F0.imprint","IMPRINT",EDGE,{"derivedFrom":subQ0}),-1.0]])]});}
            var Q30;
            {var subQ0=sQuery(id+"F0.wireOp",EDGE,"E10.23.0");Q30=makeQuery(id+"F0.imprint","IMPRINT",FACE,{"disambiguationData":[TD([[makeQuery(id+"F0.imprint","IMPRINT",EDGE,{"derivedFrom":subQ0}),-1.0]])]});}
            var Q31;
            {var subQ0=sQuery(id+"F0.wireOp",EDGE,"E10.27.0");Q31=makeQuery(id+"F0.imprint","IMPRINT",FACE,{"disambiguationData":[TD([[makeQuery(id+"F0.imprint","IMPRINT",EDGE,{"derivedFrom":subQ0}),-1.0]])]});}
            var Q32;
            {var subQ0=sQuery(id+"F0.wireOp",EDGE,"E10.31.0");Q32=makeQuery(id+"F0.imprint","IMPRINT",FACE,{"disambiguationData":[TD([[makeQuery(id+"F0.imprint","IMPRINT",EDGE,{"derivedFrom":subQ0}),-1.0]])]});}
            var Q33;
            {var subQ0=sQuery(id+"F0.wireOp",EDGE,"E10.17.0");Q33=makeQuery(id+"F0.imprint","IMPRINT",FACE,{"disambiguationData":[TD([[makeQuery(id+"F0.imprint","IMPRINT",EDGE,{"derivedFrom":subQ0}),-1.0]])]});}
            var Q34;
            {var subQ0=sQuery(id+"F0.wireOp",EDGE,"E10.32.0");Q34=makeQuery(id+"F0.imprint","IMPRINT",FACE,{"disambiguationData":[TD([[makeQuery(id+"F0.imprint","IMPRINT",EDGE,{"derivedFrom":subQ0}),-1.0]])]});}
            var Q35;
            {var subQ0=sQuery(id+"F0.wireOp",EDGE,"E10.33.0");Q35=makeQuery(id+"F0.imprint","IMPRINT",FACE,{"disambiguationData":[TD([[makeQuery(id+"F0.imprint","IMPRINT",EDGE,{"derivedFrom":subQ0}),-1.0]])]});}
            var Q36;
            {var subQ0=sQuery(id+"F0.wireOp",EDGE,"E10.34.0");Q36=makeQuery(id+"F0.imprint","IMPRINT",FACE,{"disambiguationData":[TD([[makeQuery(id+"F0.imprint","IMPRINT",EDGE,{"derivedFrom":subQ0}),-1.0]])]});}
            var Q37;
            {var subQ0=sQuery(id+"F0.wireOp",EDGE,"E10.29.0");Q37=makeQuery(id+"F0.imprint","IMPRINT",FACE,{"disambiguationData":[TD([[makeQuery(id+"F0.imprint","IMPRINT",EDGE,{"derivedFrom":subQ0}),-1.0]])]});}
            var Q38;
            {var subQ0=sQuery(id+"F0.wireOp",EDGE,"E10.6.0");Q38=makeQuery(id+"F0.imprint","IMPRINT",FACE,{"disambiguationData":[TD([[makeQuery(id+"F0.imprint","IMPRINT",EDGE,{"derivedFrom":subQ0}),-1.0]])]});}
            var Q39;
            {var subQ0=sQuery(id+"F0.wireOp",EDGE,"E10.15.0");Q39=makeQuery(id+"F0.imprint","IMPRINT",FACE,{"disambiguationData":[TD([[makeQuery(id+"F0.imprint","IMPRINT",EDGE,{"derivedFrom":subQ0}),-1.0]])]});}
            var Q40;
            {var subQ0=sQuery(id+"F0.wireOp",EDGE,"E10.22.0");Q40=makeQuery(id+"F0.imprint","IMPRINT",FACE,{"disambiguationData":[TD([[makeQuery(id+"F0.imprint","IMPRINT",EDGE,{"derivedFrom":subQ0}),-1.0]])]});}
            var Q41;
            {var subQ0=sQuery(id+"F0.wireOp",EDGE,"E10.19.0");Q41=makeQuery(id+"F0.imprint","IMPRINT",FACE,{"disambiguationData":[TD([[makeQuery(id+"F0.imprint","IMPRINT",EDGE,{"derivedFrom":subQ0}),-1.0]])]});}
            var Q42;
            {var subQ0=sQuery(id+"F0.wireOp",EDGE,"E10.21.0");Q42=makeQuery(id+"F0.imprint","IMPRINT",FACE,{"disambiguationData":[TD([[makeQuery(id+"F0.imprint","IMPRINT",EDGE,{"derivedFrom":subQ0}),-1.0]])]});}
            var Q43;
            {var subQ0=sQuery(id+"F0.wireOp",EDGE,"E10.18.0");Q43=makeQuery(id+"F0.imprint","IMPRINT",FACE,{"disambiguationData":[TD([[makeQuery(id+"F0.imprint","IMPRINT",EDGE,{"derivedFrom":subQ0}),-1.0]])]});}
            extrude(context, id + "F1", {"entities" : qUnion([Q0, Q1, Q2, Q3, Q4, Q5, Q6, Q7, Q8, Q9, Q10, Q11, Q12, Q13, Q14, Q15, Q16, Q17, Q18, Q19, Q20, Q21, Q22, Q23, Q24, Q25, Q26, Q27, Q28, Q29, Q30, Q31, Q32, Q33, Q34, Q35, Q36, Q37, Q38, Q39, Q40, Q41, Q42, Q43]), "endBound" : BoundingType.SYMMETRIC, "depth" : 10.24 * mm, "offsetDistance" : 25 * mm});
        }
        {
            var Q0;
            Q0=makeQuery(id+"F0.imprint","IMPRINT",FACE,{"disambiguationData":[TD([[makeQuery(id+"F0.imprint","IMPRINT",EDGE,{"derivedFrom":sQuery(id+"F0.wireOp",EDGE,"E11.left")}),1.0]])]});
            var Q1;
            Q1=makeQuery(id+"F0.imprint","IMPRINT",FACE,{"disambiguationData":[TD([[makeQuery(id+"F0.imprint","IMPRINT",EDGE,{"derivedFrom":sQuery(id+"F0.wireOp",EDGE,"E11.right")}),-1.0]])]});
            var Q2;
            {var subQ0=sQuery(id+"F0.wireOp",EDGE,"E16.4.3");Q2=makeQuery(id+"F0.imprint","IMPRINT",FACE,{"disambiguationData":[TD([[makeQuery(id+"F0.imprint","IMPRINT",EDGE,{"derivedFrom":subQ0}),1.0]])]});}
            var Q3;
            {var subQ0=sQuery(id+"F0.wireOp",EDGE,"E16.3.3");Q3=makeQuery(id+"F0.imprint","IMPRINT",FACE,{"disambiguationData":[TD([[makeQuery(id+"F0.imprint","IMPRINT",EDGE,{"derivedFrom":subQ0}),1.0]])]});}
            var Q4;
            {var subQ3=sQuery(id+"F0.wireOp",EDGE,"E16.2.3");Q4=makeQuery(id+"F0.imprint","IMPRINT",FACE,{"disambiguationData":[TD([[makeQuery(id+"F0.imprint","IMPRINT",EDGE,{"derivedFrom":subQ3}),1.0]])]});}
            var Q5;
            {var subQ0=sQuery(id+"F0.wireOp",EDGE,"E16.1.3");Q5=makeQuery(id+"F0.imprint","IMPRINT",FACE,{"disambiguationData":[TD([[makeQuery(id+"F0.imprint","IMPRINT",EDGE,{"derivedFrom":subQ0}),1.0]])]});}
            extrude(context, id + "F2", {"entities" : qUnion([Q0, Q1, Q2, Q3, Q4, Q5]), "operationType" : NewBodyOperationType.ADD, "endBound" : BoundingType.SYMMETRIC, "depth" : 6.83 * mm, "offsetDistance" : 25 * mm});
        }
        {
            var Q0;
            Q0=qCreatedBy(makeId("Top.planeOp"),FACE);
            var sketch = newSketch(context, id + "F3", { "sketchPlane" : qUnion([Q0])});
            skCircle(sketch, "E17.0", {"center": v(0, 0) * mm, "radius": 4.2 * mm});
            skCircle(sketch, "E18.0", {"center": v(0, 0) * mm, "radius": 7 * mm});
            skSolve(sketch);
        }
        {
            var Q0;
            Q0 = qSketchRegion(id + "F3", true);
            extrude(context, id + "F4", {"entities" : qUnion([Q0]), "operationType" : NewBodyOperationType.ADD, "depth" : 8.08 * mm, "offsetDistance" : 25 * mm});
        }
        {
            var Q0;
            Q0 = qSketchRegion(id + "F3", true);
            extrude(context, id + "F5", {"entities" : qUnion([Q0]), "operationType" : NewBodyOperationType.ADD, "oppositeDirection" : true, "depth" : 6.28 * mm, "offsetDistance" : 25 * mm});
        }
    });
